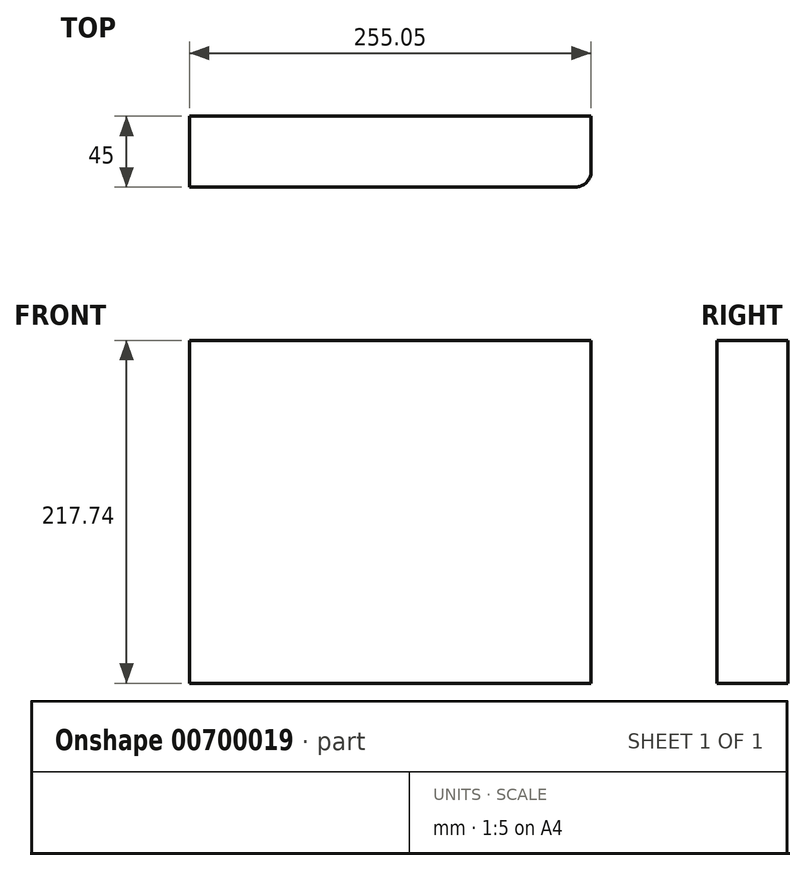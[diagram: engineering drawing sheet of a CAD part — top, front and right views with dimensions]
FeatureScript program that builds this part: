
annotation { "Feature Type Name" : "Feature", "Feature Type Description" : "" }
export const myFeature = defineFeature(function(context is Context, id is Id, definition is map)
    precondition{}
    {
        {
            var Q0;
            Q0=qCreatedBy(makeId("Front.planeOp"),FACE);
            var sketch = newSketch(context, id + "F0", { "sketchPlane" : qUnion([Q0])});
            skLineSegment(sketch, "E0.bottom", {"start": v(97.5, -74.06) * mm, "end": v(-157.54, -74.06) * mm});
            skLineSegment(sketch, "E0.top", {"start": v(97.5, 143.68) * mm, "end": v(-157.54, 143.68) * mm});
            skLineSegment(sketch, "E0.left", {"start": v(97.5, -74.06) * mm, "end": v(97.5, 143.68) * mm});
            skLineSegment(sketch, "E0.right", {"start": v(-157.54, -74.06) * mm, "end": v(-157.54, 143.68) * mm});
            skPoint(sketch, "E0.middle", {"position": v(-30.02, 34.81) * mm});
            skSolve(sketch);
        }
        {
            var Q0;
            Q0=makeQuery(id+"F0.imprint","IMPRINT",FACE,{"disambiguationData":[TD([[makeQuery(id+"F0.imprint","IMPRINT",EDGE,{"derivedFrom":sQuery(id+"F0.wireOp",EDGE,"E0.bottom")}),-1.0]])]});
            extrude(context, id + "F1", {"entities" : qUnion([Q0]), "depth" : 45 * mm, "offsetDistance" : 25.4 * mm});
        }
        {
            var Q0;
            Q0=makeQuery(id+"F1.opExtrude","CAP_EDGE",EDGE,{"disambiguationData":[OSD([sQuery(id+"F0.wireOp",EDGE,"E0.left")])],"isStart":false});
            fillet(context, id + "F2", {"entities" : qUnion([Q0]), "radius" : 10 * mm, "tangentPropagation" : true, "allowEdgeOverflow" : false});
        }
        {
            var Q0;
            Q0=makeQuery(id+"F1.opExtrude","CAP_FACE",FACE,{"disambiguationData":[OSD([sQuery(id+"F0.wireOp",EDGE,"E0.bottom"),sQuery(id+"F0.wireOp",EDGE,"E0.top"),sQuery(id+"F0.wireOp",EDGE,"E0.left"),sQuery(id+"F0.wireOp",EDGE,"E0.right")])],"isStart":false});
            var sketch = newSketch(context, id + "F3", { "sketchPlane" : qUnion([Q0])});
            skCircle(sketch, "E1", {"center": v(-76.15, 63.18) * mm, "radius": 19.57 * mm});
            skCircle(sketch, "E2", {"center": v(160.5, 2.88) * mm, "radius": 43.23 * mm});
            skSolve(sketch);
        }
        {
            var Q0;
            Q0=sQuery(id+"F3.wireOp",EDGE,"E1");
            extrude(context, id + "F4", {"bodyType" : ToolBodyType.SURFACE, "surfaceEntities" : qUnion([Q0]), "depth" : 45 * mm, "offsetDistance" : 25.4 * mm});
        }
    });
